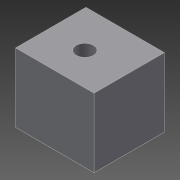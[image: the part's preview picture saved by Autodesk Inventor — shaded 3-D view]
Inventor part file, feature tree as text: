
AUTODESK INVENTOR PART (.ipt)
format: ipt  version: 2014 SP1 (Build 180222100, 222)  size: 72,192 bytes
history: native  units: in
note: dims shown in document units (in); Inventor stores cm internally (conversion verified against a paired STEP export)
features: other x3, extrude x1, hole x1, sketch x1
ambient origin geometry x5: Origin, X Axis, Y Axis, Z Axis, Center Point
bodies: Solid1 (feature_tree)
feature tree (6):
  extrude  "Extrusion1"  Depth=1.0in
  hole  "Hole1"  [1 undecoded]
  other  "Right (YZ)"
  other  "Top (XZ)"
  other  "Front (XY)"
  sketch  "Sketch1"  dims[d0=1.0in d1=0.0in d2=1.0in d3=1.0in d4=0.25in d5=0.75in d6=0.375in d7=0.25in d8=0.5635in d9=1.0in d10=0.8108in]
note: 1 required parameter value undecoded (feature->parameter linkage not recoverable at this tier; creation-order binding heuristic only, values carry confidence <= 0.55)
